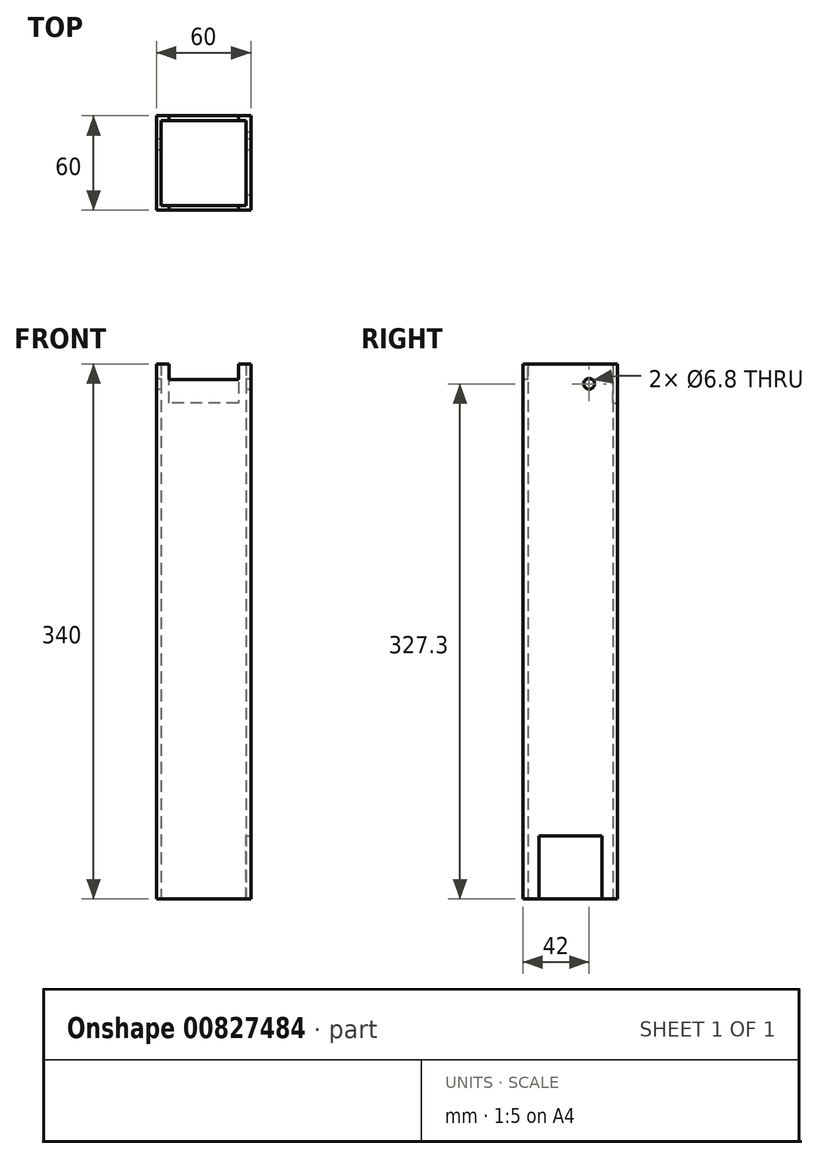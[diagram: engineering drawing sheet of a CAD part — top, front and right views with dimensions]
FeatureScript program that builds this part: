
annotation { "Feature Type Name" : "Feature", "Feature Type Description" : "" }
export const myFeature = defineFeature(function(context is Context, id is Id, definition is map)
    precondition{}
    {
        {
            var Q0;
            Q0=qCreatedBy(makeId("Top.planeOp"),FACE);
            var sketch = newSketch(context, id + "F0", { "sketchPlane" : qUnion([Q0])});
            skLineSegment(sketch, "E0.bottom", {"start": v(0, 0) * mm, "end": v(60, 0) * mm});
            skLineSegment(sketch, "E0.top", {"start": v(0, 60) * mm, "end": v(60, 60) * mm});
            skLineSegment(sketch, "E0.left", {"start": v(0, 0) * mm, "end": v(0, 60) * mm});
            skLineSegment(sketch, "E0.right", {"start": v(60, 0) * mm, "end": v(60, 60) * mm});
            skLineSegment(sketch, "E1.0", {"start": v(3, 3) * mm, "end": v(3, 57) * mm});
            skLineSegment(sketch, "E1.1", {"start": v(3, 3) * mm, "end": v(57, 3) * mm});
            skLineSegment(sketch, "E1.2", {"start": v(57, 3) * mm, "end": v(57, 57) * mm});
            skLineSegment(sketch, "E1.3", {"start": v(3, 57) * mm, "end": v(57, 57) * mm});
            skSolve(sketch);
        }
        {
            var Q0;
            Q0 = qSketchRegion(id + "F0", true);
            extrude(context, id + "F1", {"entities" : qUnion([Q0]), "depth" : 340 * mm, "offsetDistance" : 25 * mm});
        }
        {
            var Q0;
            Q0=makeQuery(id+"F1.opExtrude","SWEPT_FACE",FACE,{"disambiguationData":[OSD([sQuery(id+"F0.wireOp",EDGE,"E0.right")])]});
            var sketch = newSketch(context, id + "F2", { "sketchPlane" : qUnion([Q0])});
            skLineSegment(sketch, "E2", {"start": v(10, 0) * mm, "end": v(10, 40) * mm});
            skLineSegment(sketch, "E3", {"start": v(10, 40) * mm, "end": v(50, 40) * mm});
            skLineSegment(sketch, "E4", {"start": v(50, 40) * mm, "end": v(50, 0) * mm});
            skSolve(sketch);
        }
        {
            var Q0;
            {var subQ0=sQuery(id+"F2.wireOp",EDGE,"E2");Q0=makeQuery(id+"F2.imprint","IMPRINT",FACE,{"disambiguationData":[TD([[makeQuery(id+"F2.imprint","IMPRINT",EDGE,{"derivedFrom":subQ0}),-1.0]])]});}
            extrude(context, id + "F3", {"entities" : qUnion([Q0]), "operationType" : NewBodyOperationType.REMOVE, "oppositeDirection" : true, "depth" : 3 * mm, "offsetDistance" : 25 * mm});
        }
        {
            var Q0;
            Q0=makeQuery(id+"F1.opExtrude","SWEPT_FACE",FACE,{"disambiguationData":[OSD([sQuery(id+"F0.wireOp",EDGE,"E0.top")])]});
            var sketch = newSketch(context, id + "F4", { "sketchPlane" : qUnion([Q0])});
            skLineSegment(sketch, "E5", {"start": v(-52, 342) * mm, "end": v(-52, 315) * mm});
            skLineSegment(sketch, "E6", {"start": v(-52, 315) * mm, "end": v(-8, 315) * mm});
            skLineSegment(sketch, "E7", {"start": v(-8, 315) * mm, "end": v(-8, 340) * mm});
            skSolve(sketch);
        }
        {
            var Q0;
            {var subQ0=sQuery(id+"F4.wireOp",EDGE,"E5");Q0=makeQuery(id+"F4.imprint","IMPRINT",FACE,{"disambiguationData":[TD([[makeQuery(id+"F4.imprint","IMPRINT",EDGE,{"derivedFrom":subQ0}),1.0]])]});}
            extrude(context, id + "F5", {"entities" : qUnion([Q0]), "operationType" : NewBodyOperationType.REMOVE, "oppositeDirection" : true, "depth" : 3 * mm, "offsetDistance" : 25 * mm});
        }
        {
            var Q0;
            Q0=makeQuery(id+"F1.opExtrude","SWEPT_FACE",FACE,{"disambiguationData":[OSD([sQuery(id+"F0.wireOp",EDGE,"E0.right")])]});
            var sketch = newSketch(context, id + "F6", { "sketchPlane" : qUnion([Q0])});
            skCircle(sketch, "E8", {"center": v(42, 327.3) * mm, "radius": 12.7 * mm, "construction": true});
            skSolve(sketch);
        }
        {
            var Q0;
            Q0=sQuery(id+"F6.wireOp",VERTEX,"E8.center");
            var Q1;
            Q1=makeQuery(id+"F1.opExtrude","SWEPT_BODY",BODY,{"disambiguationData":[OSD([sQuery(id+"F0.wireOp",EDGE,"E0.bottom"),sQuery(id+"F0.wireOp",EDGE,"E0.top"),sQuery(id+"F0.wireOp",EDGE,"E0.left"),sQuery(id+"F0.wireOp",EDGE,"E0.right"),sQuery(id+"F0.wireOp",EDGE,"E1.0"),sQuery(id+"F0.wireOp",EDGE,"E1.1"),sQuery(id+"F0.wireOp",EDGE,"E1.2"),sQuery(id+"F0.wireOp",EDGE,"E1.3")])]});
            hole(context, id + "F7", {"style" : HoleStyle.SIMPLE, "endStyle" : HoleEndStyle.THROUGH, "standardTappedOrClearance" : lookupTablePath({ "standard" : "ISO", "engagement" : "75%", "pitch" : "1.25 mm", "size" : "M8", "type" : "Tapped" }), "standardBlindInLast" : lookupTablePath({ "standard" : "ISO", "engagement" : "75%", "pitch" : "1.25 mm", "size" : "M8", "type" : "Tapped" }), "holeDiameter" : 6.8 * mm, "majorDiameter" : 8 * mm, "showTappedDepth" : true, "isTappedThrough" : true, "tappedDepth" : 12 * mm, "tapClearance" : 3, "locations" : qUnion([Q0]), "scope" : qUnion([Q1])});
        }
        {
            var Q0;
            Q0=makeQuery(id+"F1.opExtrude","SWEPT_FACE",FACE,{"disambiguationData":[OSD([sQuery(id+"F0.wireOp",EDGE,"E0.bottom")])]});
            var sketch = newSketch(context, id + "F8", { "sketchPlane" : qUnion([Q0])});
            skLineSegment(sketch, "E9.bottom", {"start": v(8, 340) * mm, "end": v(52, 340) * mm});
            skLineSegment(sketch, "E9.top", {"start": v(8, 330) * mm, "end": v(52, 330) * mm});
            skLineSegment(sketch, "E9.left", {"start": v(8, 340) * mm, "end": v(8, 330) * mm});
            skLineSegment(sketch, "E9.right", {"start": v(52, 340) * mm, "end": v(52, 330) * mm});
            skSolve(sketch);
        }
        {
            var Q0;
            Q0 = qSketchRegion(id + "F8", true);
            extrude(context, id + "F9", {"entities" : qUnion([Q0]), "operationType" : NewBodyOperationType.REMOVE, "oppositeDirection" : true, "depth" : 25 * mm, "offsetDistance" : 25 * mm});
        }
    });
